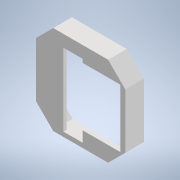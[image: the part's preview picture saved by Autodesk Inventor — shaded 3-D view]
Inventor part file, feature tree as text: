
AUTODESK INVENTOR PART (.ipt)
format: ipt  version: 2021.2 (Build 252289000, 289)  size: 188,416 bytes
history: native  units: mm
features: reference x13, other x3, extrude x3, sketch x3, projected_geometry x1
ambient origin geometry x8: Origin, YZ Plane, XZ Plane, XY Plane, X Axis, Y Axis, Z Axis, Center Point
bodies: Body1 (feature_tree)
feature tree (23):
  other  "Твердое тело1"
  extrude  "Выдавливание1"  Depth=1.5mm
  extrude  "Выдавливание2"  Depth=1.0mm
  extrude  "Выдавливание3"  Depth=0.5mm
  sketch  "Эскиз1"
  reference  "Ссылка1"
  reference  "Ссылка2"
  reference  "Ссылка3"
  reference  "Ссылка4"
  reference  "Ссылка5"
  reference  "Ссылка6"
  reference  "Ссылка7"
  reference  "Ссылка8"
  reference  "Ссылка9"
  reference  "Ссылка10"
  reference  "Ссылка11"
  reference  "Ссылка12"
  reference  "Ссылка13"
  sketch  "Эскиз2"
  projected_geometry  "Спроецированная петля1"
  sketch  "Эскиз3"
  other  "Сборка1"
  other  "Плата печатная2:1"
